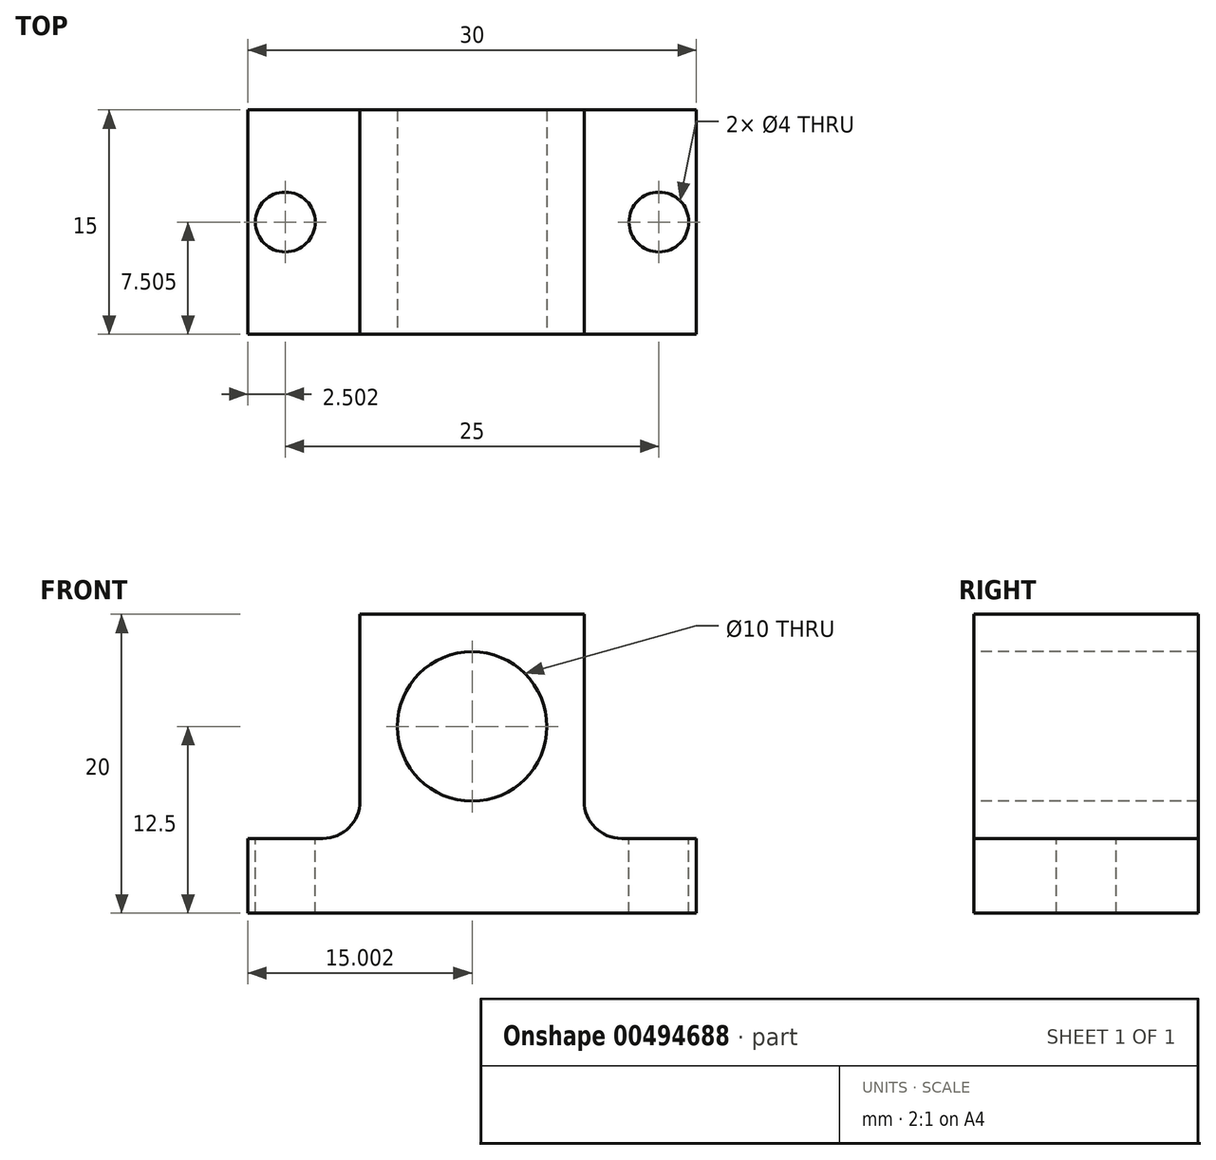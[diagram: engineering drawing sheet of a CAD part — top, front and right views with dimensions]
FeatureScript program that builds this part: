
annotation { "Feature Type Name" : "Feature", "Feature Type Description" : "" }
export const myFeature = defineFeature(function(context is Context, id is Id, definition is map)
    precondition{}
    {
        {
            var Q0;
            Q0=qCreatedBy(makeId("Top.planeOp"),FACE);
            var sketch = newSketch(context, id + "F0", { "sketchPlane" : qUnion([Q0])});
            skLineSegment(sketch, "E0.bottom", {"start": v(-66.16, -68.47) * mm, "end": v(-36.16, -68.47) * mm});
            skLineSegment(sketch, "E0.top", {"start": v(-66.16, -53.47) * mm, "end": v(-36.16, -53.47) * mm});
            skLineSegment(sketch, "E0.left", {"start": v(-66.16, -68.47) * mm, "end": v(-66.16, -53.47) * mm});
            skLineSegment(sketch, "E0.right", {"start": v(-36.16, -68.47) * mm, "end": v(-36.16, -53.47) * mm});
            skSolve(sketch);
        }
        {
            var Q0;
            Q0 = qSketchRegion(id + "F0", true);
            extrude(context, id + "F1", {"entities" : qUnion([Q0]), "depth" : 20 * mm});
        }
        {
            var Q0;
            Q0=makeQuery(id+"F1.opExtrude","SWEPT_FACE",FACE,{"disambiguationData":[OSD([sQuery(id+"F0.wireOp",EDGE,"E0.bottom")])]});
            var sketch = newSketch(context, id + "F2", { "sketchPlane" : qUnion([Q0])});
            skLineSegment(sketch, "E1", {"start": v(-66.16, 20) * mm, "end": v(-61.16, 20) * mm});
            skLineSegment(sketch, "E2", {"start": v(-61.16, 20) * mm, "end": v(-61.16, 0) * mm});
            skSolve(sketch);
        }
        {
            var Q0;
            Q0=makeQuery(id+"F2.imprint","IMPRINT",FACE,{"disambiguationData":[TD([[makeQuery(id+"F2.imprint","IMPRINT",EDGE,{"derivedFrom":sQuery(id+"F2.wireOp",EDGE,"E1")}),-1.0]])]});
            extrude(context, id + "F3", {"entities" : qUnion([Q0]), "operationType" : NewBodyOperationType.REMOVE, "oppositeDirection" : true, "depth" : 25 * mm});
        }
        {
            var Q0;
            Q0=makeQuery(id+"F3.boolean.opBoolean","COPY",FACE,{"derivedFrom":makeQuery(id+"F3.opExtrude","SWEPT_FACE",FACE,{"disambiguationData":[OSD([sQuery(id+"F2.wireOp",EDGE,"E2")])]})});
            var sketch = newSketch(context, id + "F4", { "sketchPlane" : qUnion([Q0])});
            skLineSegment(sketch, "E3", {"start": v(68.47, 0) * mm, "end": v(68.47, 5) * mm});
            skLineSegment(sketch, "E4", {"start": v(68.47, 5) * mm, "end": v(53.47, 5) * mm});
            skSolve(sketch);
        }
        {
            var Q0;
            Q0=makeQuery(id+"F4.imprint","IMPRINT",FACE,{"disambiguationData":[TD([[makeQuery(id+"F4.imprint","IMPRINT",EDGE,{"derivedFrom":sQuery(id+"F4.wireOp",EDGE,"E3")}),-1.0]])]});
            extrude(context, id + "F5", {"entities" : qUnion([Q0]), "operationType" : NewBodyOperationType.ADD, "depth" : 5 * mm});
        }
        {
            var Q0;
            Q0=makeQuery(id+"F5.boolean.opBoolean","MERGE",FACE,{"derivedFrom":[makeQuery(id+"F1.opExtrude","SWEPT_FACE",FACE,{"disambiguationData":[OSD([sQuery(id+"F0.wireOp",EDGE,"E0.bottom")])]}),makeQuery(id+"F5.opExtrude","SWEPT_FACE",FACE,{"disambiguationData":[OSD([sQuery(id+"F4.wireOp",EDGE,"E3")])]})]});
            var sketch = newSketch(context, id + "F6", { "sketchPlane" : qUnion([Q0])});
            skLineSegment(sketch, "E5", {"start": v(-36.16, 20) * mm, "end": v(-41.16, 20) * mm});
            skLineSegment(sketch, "E6", {"start": v(-41.16, 20) * mm, "end": v(-41.16, 0) * mm});
            skSolve(sketch);
        }
        {
            var Q0;
            Q0=makeQuery(id+"F6.imprint","IMPRINT",FACE,{"disambiguationData":[TD([[makeQuery(id+"F6.imprint","IMPRINT",EDGE,{"derivedFrom":sQuery(id+"F6.wireOp",EDGE,"E5")}),-1.0]])]});
            extrude(context, id + "F7", {"entities" : qUnion([Q0]), "operationType" : NewBodyOperationType.REMOVE, "oppositeDirection" : true, "depth" : 25 * mm});
        }
        {
            var Q0;
            Q0=makeQuery(id+"F7.boolean.opBoolean","COPY",FACE,{"derivedFrom":makeQuery(id+"F7.opExtrude","SWEPT_FACE",FACE,{"disambiguationData":[OSD([sQuery(id+"F6.wireOp",EDGE,"E6")])]})});
            var sketch = newSketch(context, id + "F8", { "sketchPlane" : qUnion([Q0])});
            skLineSegment(sketch, "E7", {"start": v(-68.47, 0) * mm, "end": v(-68.47, 5) * mm});
            skLineSegment(sketch, "E8", {"start": v(-68.47, 5) * mm, "end": v(-53.47, 5) * mm});
            skSolve(sketch);
        }
        {
            var Q0;
            Q0=makeQuery(id+"F8.imprint","IMPRINT",FACE,{"disambiguationData":[TD([[makeQuery(id+"F8.imprint","IMPRINT",EDGE,{"derivedFrom":sQuery(id+"F8.wireOp",EDGE,"E7")}),1.0]])]});
            extrude(context, id + "F9", {"entities" : qUnion([Q0]), "operationType" : NewBodyOperationType.ADD, "depth" : 5 * mm});
        }
        {
            var Q0;
            Q0=makeQuery(id+"F1.opExtrude","CAP_FACE",FACE,{"disambiguationData":[OSD([sQuery(id+"F0.wireOp",EDGE,"E0.bottom"),sQuery(id+"F0.wireOp",EDGE,"E0.top"),sQuery(id+"F0.wireOp",EDGE,"E0.left"),sQuery(id+"F0.wireOp",EDGE,"E0.right")])],"isStart":false});
            var sketch = newSketch(context, id + "F10", { "sketchPlane" : qUnion([Q0])});
            skLineSegment(sketch, "E9", {"start": v(-41.16, -68.47) * mm, "end": v(-43.66, -68.47) * mm});
            skLineSegment(sketch, "E10", {"start": v(-61.16, -68.47) * mm, "end": v(-58.66, -68.47) * mm});
            skLineSegment(sketch, "E11", {"start": v(-58.66, -68.47) * mm, "end": v(-58.66, -53.47) * mm});
            skLineSegment(sketch, "E12", {"start": v(-43.66, -68.47) * mm, "end": v(-43.66, -53.47) * mm});
            skSolve(sketch);
        }
        {
            var Q0;
            Q0=makeQuery(id+"F10.imprint","IMPRINT",FACE,{"disambiguationData":[TD([[makeQuery(id+"F10.imprint","IMPRINT",EDGE,{"derivedFrom":sQuery(id+"F10.wireOp",EDGE,"E10")}),1.0]])]});
            var Q1;
            Q1=makeQuery(id+"F10.imprint","IMPRINT",FACE,{"disambiguationData":[TD([[makeQuery(id+"F10.imprint","IMPRINT",EDGE,{"derivedFrom":sQuery(id+"F10.wireOp",EDGE,"E9")}),1.0]])]});
            extrude(context, id + "F11", {"entities" : qUnion([Q0, Q1]), "operationType" : NewBodyOperationType.REMOVE, "oppositeDirection" : true, "depth" : 15 * mm});
        }
        {
            var Q0;
            Q0=makeQuery(id+"F11.boolean.opBoolean","COPY",EDGE,{"derivedFrom":makeQuery(id+"F11.opExtrude","CAP_EDGE",EDGE,{"disambiguationData":[OSD([sQuery(id+"F10.wireOp",EDGE,"E12")])],"isStart":false})});
            fillet(context, id + "F12", {"entities" : qUnion([Q0]), "radius" : 2.5 * mm, "tangentPropagation" : true, "allowEdgeOverflow" : false});
        }
        {
            var Q0;
            Q0=makeQuery(id+"F11.boolean.opBoolean","COPY",EDGE,{"derivedFrom":makeQuery(id+"F11.opExtrude","CAP_EDGE",EDGE,{"disambiguationData":[OSD([sQuery(id+"F10.wireOp",EDGE,"E11")])],"isStart":false})});
            fillet(context, id + "F13", {"entities" : qUnion([Q0]), "radius" : 2.5 * mm, "tangentPropagation" : true, "allowEdgeOverflow" : false});
        }
        {
            var Q0;
            Q0=makeQuery(id+"F9.boolean.opBoolean","MERGE",FACE,{"derivedFrom":[makeQuery(id+"F5.boolean.opBoolean","MERGE",FACE,{"derivedFrom":[makeQuery(id+"F1.opExtrude","SWEPT_FACE",FACE,{"disambiguationData":[OSD([sQuery(id+"F0.wireOp",EDGE,"E0.bottom")])]}),makeQuery(id+"F5.opExtrude","SWEPT_FACE",FACE,{"disambiguationData":[OSD([sQuery(id+"F4.wireOp",EDGE,"E3")])]})]}),makeQuery(id+"F9.opExtrude","SWEPT_FACE",FACE,{"disambiguationData":[OSD([sQuery(id+"F8.wireOp",EDGE,"E7")])]})]});
            var sketch = newSketch(context, id + "F14", { "sketchPlane" : qUnion([Q0])});
            skCircle(sketch, "E13", {"center": v(-51.16, 12.5) * mm, "radius": 5 * mm});
            skSolve(sketch);
        }
        {
            var Q0;
            Q0=makeQuery(id+"F14.imprint","IMPRINT",FACE,{"disambiguationData":[TD([[makeQuery(id+"F14.imprint","IMPRINT",EDGE,{"derivedFrom":sQuery(id+"F14.wireOp",EDGE,"E13")}),1.0]])]});
            extrude(context, id + "F15", {"entities" : qUnion([Q0]), "operationType" : NewBodyOperationType.REMOVE, "oppositeDirection" : true, "depth" : 20 * mm});
        }
        {
            var Q0;
            Q0=makeQuery(id+"F11.boolean.opBoolean","MERGE",FACE,{"derivedFrom":[makeQuery(id+"F9.opExtrude","SWEPT_FACE",FACE,{"disambiguationData":[OSD([sQuery(id+"F8.wireOp",EDGE,"E8")])]}),makeQuery(id+"F11.opExtrude","CAP_FACE",FACE,{"disambiguationData":[OSD([sQuery(id+"F0.wireOp",EDGE,"E0.bottom"),sQuery(id+"F0.wireOp",EDGE,"E0.top"),sQuery(id+"F6.wireOp",EDGE,"E5"),sQuery(id+"F6.wireOp",EDGE,"E6"),sQuery(id+"F10.wireOp",EDGE,"E9"),sQuery(id+"F10.wireOp",EDGE,"E12")])],"isStart":false})]});
            var sketch = newSketch(context, id + "F16", { "sketchPlane" : qUnion([Q0])});
            skCircle(sketch, "E14", {"center": v(-38.66, -60.97) * mm, "radius": 2 * mm});
            skSolve(sketch);
        }
        {
            var Q0;
            Q0=makeQuery(id+"F16.imprint","IMPRINT",FACE,{"disambiguationData":[TD([[makeQuery(id+"F16.imprint","IMPRINT",EDGE,{"derivedFrom":sQuery(id+"F16.wireOp",EDGE,"E14")}),1.0]])]});
            extrude(context, id + "F17", {"entities" : qUnion([Q0]), "operationType" : NewBodyOperationType.REMOVE, "oppositeDirection" : true, "depth" : 25 * mm});
        }
        {
            var Q0;
            Q0=makeQuery(id+"F11.boolean.opBoolean","MERGE",FACE,{"derivedFrom":[makeQuery(id+"F5.opExtrude","SWEPT_FACE",FACE,{"disambiguationData":[OSD([sQuery(id+"F4.wireOp",EDGE,"E4")])]}),makeQuery(id+"F11.opExtrude","CAP_FACE",FACE,{"disambiguationData":[OSD([sQuery(id+"F0.wireOp",EDGE,"E0.bottom"),sQuery(id+"F0.wireOp",EDGE,"E0.top"),sQuery(id+"F2.wireOp",EDGE,"E1"),sQuery(id+"F2.wireOp",EDGE,"E2"),sQuery(id+"F10.wireOp",EDGE,"E10"),sQuery(id+"F10.wireOp",EDGE,"E11")])],"isStart":false})]});
            var sketch = newSketch(context, id + "F18", { "sketchPlane" : qUnion([Q0])});
            skCircle(sketch, "E15", {"center": v(-63.66, -60.97) * mm, "radius": 2 * mm});
            skSolve(sketch);
        }
        {
            var Q0;
            Q0=makeQuery(id+"F18.imprint","IMPRINT",FACE,{"disambiguationData":[TD([[makeQuery(id+"F18.imprint","IMPRINT",EDGE,{"derivedFrom":sQuery(id+"F18.wireOp",EDGE,"E15")}),1.0]])]});
            extrude(context, id + "F19", {"entities" : qUnion([Q0]), "operationType" : NewBodyOperationType.REMOVE, "oppositeDirection" : true, "depth" : 25 * mm});
        }
    });
